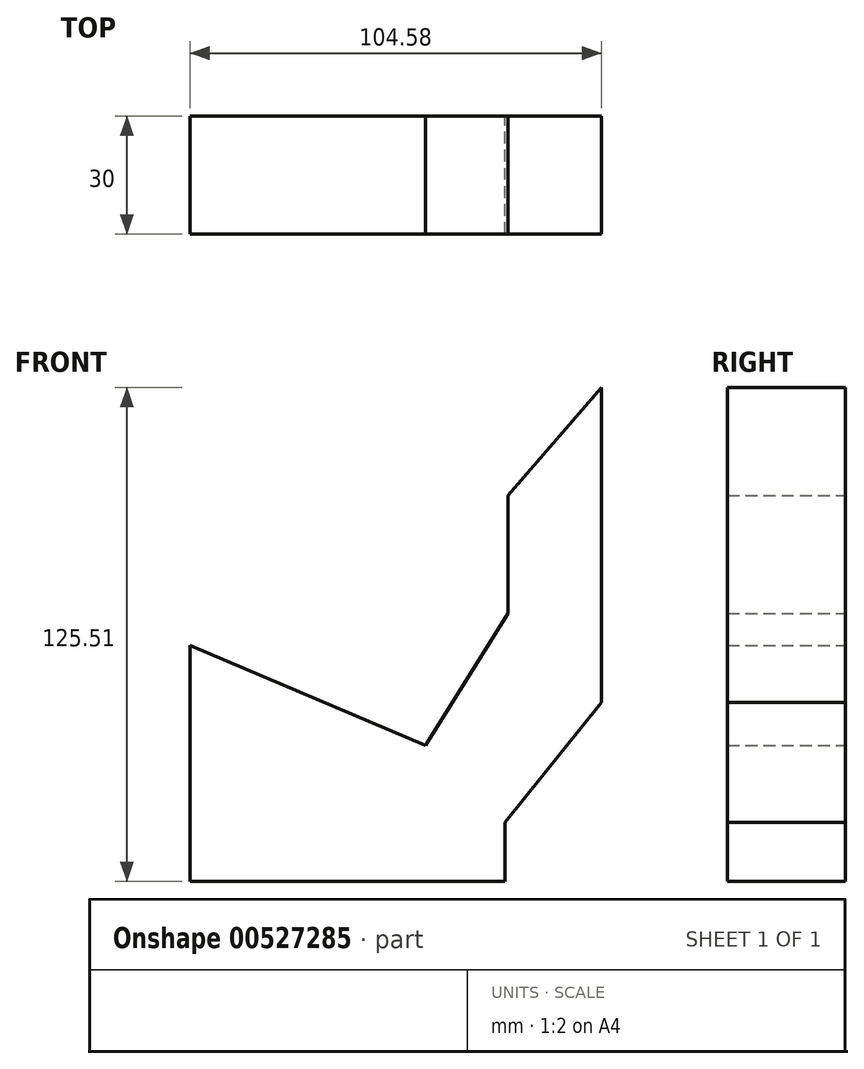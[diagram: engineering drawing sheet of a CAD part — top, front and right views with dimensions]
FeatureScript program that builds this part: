
annotation { "Feature Type Name" : "Feature", "Feature Type Description" : "" }
export const myFeature = defineFeature(function(context is Context, id is Id, definition is map)
    precondition{}
    {
        {
            var Q0;
            Q0=qCreatedBy(makeId("Front.planeOp"),FACE);
            var sketch = newSketch(context, id + "F0", { "sketchPlane" : qUnion([Q0])});
            skLineSegment(sketch, "E0", {"start": v(0, 0) * mm, "end": v(0, 60) * mm});
            skLineSegment(sketch, "E1", {"start": v(0, 60) * mm, "end": v(59.83, 34.6) * mm});
            skLineSegment(sketch, "E2", {"start": v(59.83, 34.6) * mm, "end": v(80.8, 68.15) * mm});
            skLineSegment(sketch, "E3", {"start": v(80.8, 68.15) * mm, "end": v(80.8, 98.15) * mm});
            skLineSegment(sketch, "E4", {"start": v(80.8, 98.15) * mm, "end": v(104.58, 125.5) * mm});
            skLineSegment(sketch, "E5", {"start": v(0, 0) * mm, "end": v(80, 0) * mm});
            skLineSegment(sketch, "E6", {"start": v(80, 0) * mm, "end": v(80, 15) * mm});
            skLineSegment(sketch, "E7", {"start": v(104.58, 125.5) * mm, "end": v(104.58, 45.5) * mm});
            skLineSegment(sketch, "E8", {"start": v(104.58, 45.5) * mm, "end": v(80, 15) * mm});
            skLineSegment(sketch, "E9", {"start": v(80.8, 68.15) * mm, "end": v(80, 15) * mm, "construction": true});
            skSolve(sketch);
        }
        {
            var Q0;
            Q0 = qSketchRegion(id + "F0", true);
            extrude(context, id + "F1", {"entities" : qUnion([Q0]), "depth" : 30 * mm, "offsetDistance" : 25 * mm});
        }
    });
